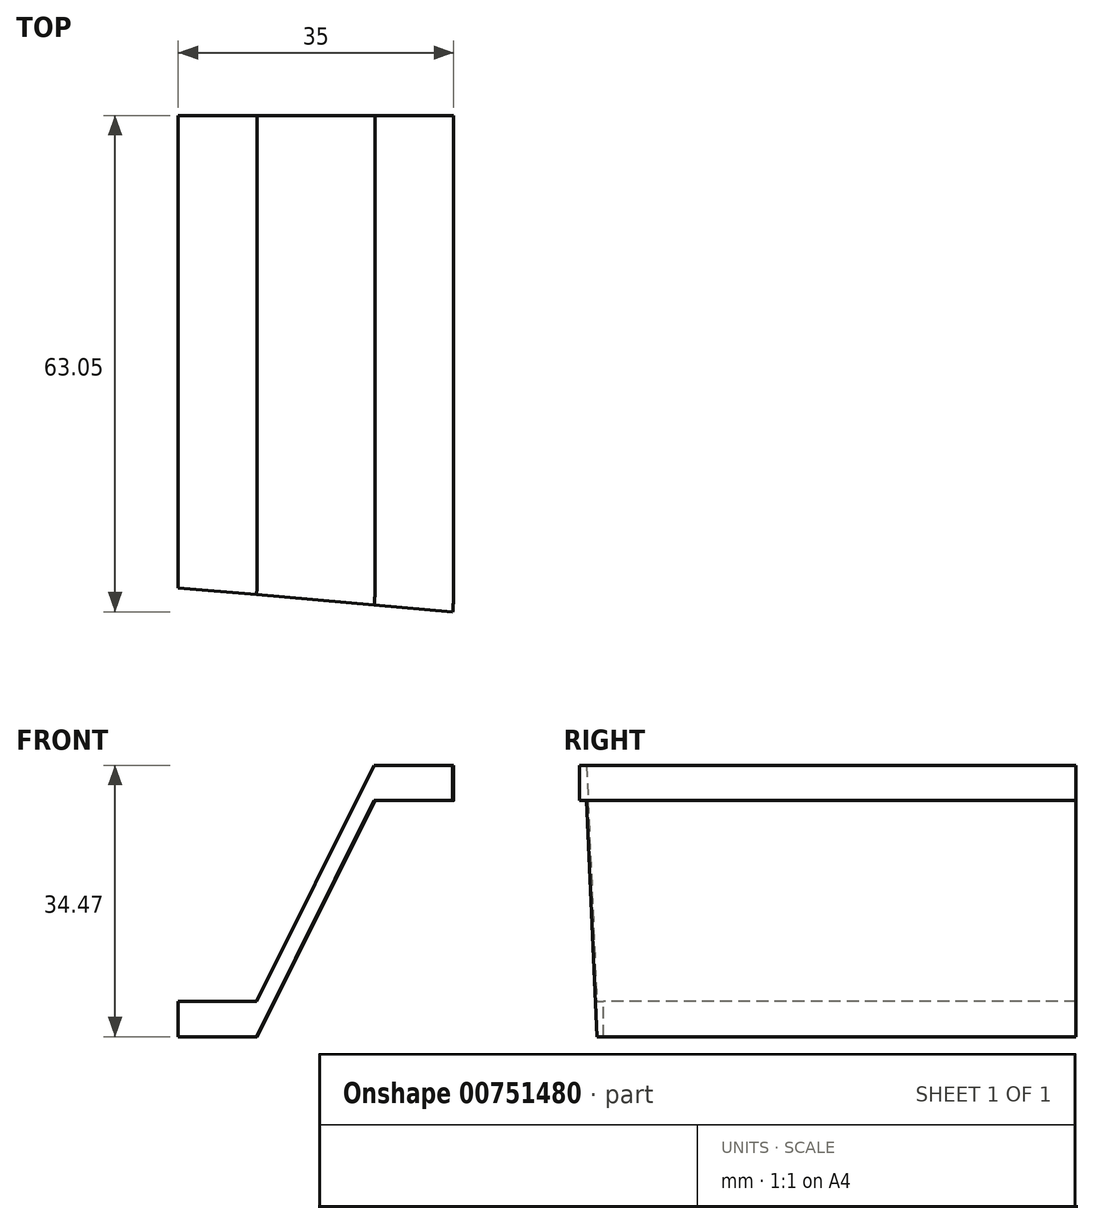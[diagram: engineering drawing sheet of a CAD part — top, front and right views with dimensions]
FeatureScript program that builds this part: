
annotation { "Feature Type Name" : "Feature", "Feature Type Description" : "" }
export const myFeature = defineFeature(function(context is Context, id is Id, definition is map)
    precondition{}
    {
        {
            var Q0;
            Q0=qCreatedBy(makeId("Front.planeOp"),FACE);
            cPlane(context, id + "F0", {"entities" : qUnion([Q0]), "cplaneType" : CPlaneType.OFFSET, "offset" : 30 * mm, "oppositeDirection" : true, "width" : 150 * mm, "height" : 150 * mm});
        }
        {
            var Q0;
            Q0=qCreatedBy(makeId("Front.planeOp"),FACE);
            cPlane(context, id + "F1", {"entities" : qUnion([Q0]), "cplaneType" : CPlaneType.OFFSET, "offset" : 30 * mm, "width" : 150 * mm, "height" : 150 * mm});
        }
        {
            var Q0;
            Q0=qCreatedBy(id+"F1.planeOp",FACE);
            var sketch = newSketch(context, id + "F2", { "sketchPlane" : qUnion([Q0])});
            skLineSegment(sketch, "E0.bottom", {"start": v(0, 34.47) * mm, "end": v(-10, 34.47) * mm});
            skLineSegment(sketch, "E0.top", {"start": v(0, 30) * mm, "end": v(-10, 30) * mm});
            skLineSegment(sketch, "E0.left", {"start": v(0, 34.47) * mm, "end": v(0, 30) * mm});
            skLineSegment(sketch, "E0.right", {"start": v(-10, 34.47) * mm, "end": v(-10, 30) * mm});
            skLineSegment(sketch, "E1.bottom", {"start": v(-25, 0) * mm, "end": v(-35, 0) * mm});
            skLineSegment(sketch, "E1.top", {"start": v(-25, 4.47) * mm, "end": v(-35, 4.47) * mm});
            skLineSegment(sketch, "E1.left", {"start": v(-25, 0) * mm, "end": v(-25, 4.47) * mm});
            skLineSegment(sketch, "E1.right", {"start": v(-35, 0) * mm, "end": v(-35, 4.47) * mm});
            skLineSegment(sketch, "E2", {"start": v(-25, 0) * mm, "end": v(-10, 30) * mm});
            skLineSegment(sketch, "E3", {"start": v(-10, 34.47) * mm, "end": v(-25, 4.47) * mm});
            skArc(sketch, "E4", {"start": v(-12.24, 30) * mm, "mid": v(-24.66, 23.05) * mm, "end": v(-22.76, 8.94) * mm});
            skArc(sketch, "E5.0", {"start": v(-11.28, 31.9) * mm, "mid": v(-26.44, 23.94) * mm, "end": v(-23.72, 7.04) * mm});
            skSolve(sketch);
        }
        {
            var Q0;
            Q0=qCreatedBy(makeId("Front.planeOp"),FACE);
            var sketch = newSketch(context, id + "F3", { "sketchPlane" : qUnion([Q0])});
            skLineSegment(sketch, "E6.bottom", {"start": v(0, 34.47) * mm, "end": v(-10, 34.47) * mm});
            skLineSegment(sketch, "E6.top", {"start": v(0, 30) * mm, "end": v(-10, 30) * mm});
            skLineSegment(sketch, "E6.left", {"start": v(0, 34.47) * mm, "end": v(0, 30) * mm});
            skLineSegment(sketch, "E6.right", {"start": v(-10, 34.47) * mm, "end": v(-10, 30) * mm});
            skLineSegment(sketch, "E7.bottom", {"start": v(-25, 0) * mm, "end": v(-35, 0) * mm});
            skLineSegment(sketch, "E7.top", {"start": v(-25, 4.47) * mm, "end": v(-35, 4.47) * mm});
            skLineSegment(sketch, "E7.left", {"start": v(-25, 0) * mm, "end": v(-25, 4.47) * mm});
            skLineSegment(sketch, "E7.right", {"start": v(-35, 0) * mm, "end": v(-35, 4.47) * mm});
            skLineSegment(sketch, "E8", {"start": v(-25, 0) * mm, "end": v(-10, 30) * mm});
            skLineSegment(sketch, "E9", {"start": v(-10, 34.47) * mm, "end": v(-25, 4.47) * mm});
            skArc(sketch, "E10", {"start": v(-13.58, 27.32) * mm, "mid": v(-20.18, 20.81) * mm, "end": v(-21.42, 11.63) * mm});
            skArc(sketch, "E11.0", {"start": v(-12.4, 29.67) * mm, "mid": v(-21.75, 21.6) * mm, "end": v(-22.6, 9.27) * mm});
            skSolve(sketch);
        }
        {
            var Q0;
            Q0=qCreatedBy(id+"F0.planeOp",FACE);
            var sketch = newSketch(context, id + "F4", { "sketchPlane" : qUnion([Q0])});
            skLineSegment(sketch, "E12.bottom", {"start": v(0, 34.47) * mm, "end": v(-10, 34.47) * mm});
            skLineSegment(sketch, "E12.top", {"start": v(0, 30) * mm, "end": v(-10, 30) * mm});
            skLineSegment(sketch, "E12.left", {"start": v(0, 34.47) * mm, "end": v(0, 30) * mm});
            skLineSegment(sketch, "E12.right", {"start": v(-10, 34.47) * mm, "end": v(-10, 30) * mm});
            skLineSegment(sketch, "E13.bottom", {"start": v(-25, 0) * mm, "end": v(-35, 0) * mm});
            skLineSegment(sketch, "E13.top", {"start": v(-25, 4.47) * mm, "end": v(-35, 4.47) * mm});
            skLineSegment(sketch, "E13.left", {"start": v(-25, 0) * mm, "end": v(-25, 4.47) * mm});
            skLineSegment(sketch, "E13.right", {"start": v(-35, 0) * mm, "end": v(-35, 4.47) * mm});
            skLineSegment(sketch, "E14", {"start": v(-25, 0) * mm, "end": v(-10, 30) * mm});
            skLineSegment(sketch, "E15", {"start": v(-10, 34.47) * mm, "end": v(-25, 4.47) * mm});
            skArc(sketch, "E16.0", {"start": v(-13.58, 27.32) * mm, "mid": v(-18.4, 19.92) * mm, "end": v(-21.42, 11.63) * mm});
            skSolve(sketch);
        }
        {
            var Q0;
            {var subQ1=sQuery(id+"F4.wireOp",EDGE,"E12.right");Q0=makeQuery(id+"F4.imprint","IMPRINT",FACE,{"disambiguationData":[TD([[makeQuery(id+"F4.imprint","IMPRINT",EDGE,{"derivedFrom":subQ1}),-1.0]])]});}
            var Q1;
            {var subQ1=sQuery(id+"F3.wireOp",EDGE,"E6.right");Q1=makeQuery(id+"F3.imprint","IMPRINT",FACE,{"disambiguationData":[TD([[makeQuery(id+"F3.imprint","IMPRINT",EDGE,{"derivedFrom":subQ1}),-1.0]])]});}
            var Q2;
            {var subQ1=sQuery(id+"F2.wireOp",EDGE,"E0.right");Q2=makeQuery(id+"F2.imprint","IMPRINT",FACE,{"disambiguationData":[TD([[makeQuery(id+"F2.imprint","IMPRINT",EDGE,{"derivedFrom":subQ1}),-1.0]])]});}
            loft(context, id + "F5", {"sheetProfilesArray" : [{ "sheetProfileEntities" : qUnion([Q0]) }, { "sheetProfileEntities" : qUnion([Q1]) }, { "sheetProfileEntities" : qUnion([Q2]) }]});
        }
        {
            var Q1;
            Q1=makeQuery(id+"F2.imprint","IMPRINT",FACE,{"disambiguationData":[TD([[makeQuery(id+"F2.imprint","IMPRINT",EDGE,{"derivedFrom":sQuery(id+"F2.wireOp",EDGE,"E0.bottom")}),1.0]])]});
            var Q2;
            Q2=makeQuery(id+"F3.imprint","IMPRINT",FACE,{"disambiguationData":[TD([[makeQuery(id+"F3.imprint","IMPRINT",EDGE,{"derivedFrom":sQuery(id+"F3.wireOp",EDGE,"E6.bottom")}),1.0]])]});
            var Q3;
            Q3=makeQuery(id+"F4.imprint","IMPRINT",FACE,{"disambiguationData":[TD([[makeQuery(id+"F4.imprint","IMPRINT",EDGE,{"derivedFrom":sQuery(id+"F4.wireOp",EDGE,"E12.bottom")}),1.0]])]});
            loft(context, id + "F6", {"operationType" : NewBodyOperationType.ADD, "sheetProfilesArray" : [{ "sheetProfileEntities" : qUnion([Q1]) }, { "sheetProfileEntities" : qUnion([Q2]) }, { "sheetProfileEntities" : qUnion([Q3]) }]});
        }
        {
            var Q1;
            Q1=makeQuery(id+"F2.imprint","IMPRINT",FACE,{"disambiguationData":[TD([[makeQuery(id+"F2.imprint","IMPRINT",EDGE,{"derivedFrom":sQuery(id+"F2.wireOp",EDGE,"E1.bottom")}),-1.0]])]});
            var Q2;
            Q2=makeQuery(id+"F3.imprint","IMPRINT",FACE,{"disambiguationData":[TD([[makeQuery(id+"F3.imprint","IMPRINT",EDGE,{"derivedFrom":sQuery(id+"F3.wireOp",EDGE,"E7.bottom")}),-1.0]])]});
            var Q3;
            Q3=makeQuery(id+"F4.imprint","IMPRINT",FACE,{"disambiguationData":[TD([[makeQuery(id+"F4.imprint","IMPRINT",EDGE,{"derivedFrom":sQuery(id+"F4.wireOp",EDGE,"E13.bottom")}),-1.0]])]});
            loft(context, id + "F7", {"operationType" : NewBodyOperationType.ADD, "sheetProfilesArray" : [{ "sheetProfileEntities" : qUnion([Q1]) }, { "sheetProfileEntities" : qUnion([Q2]) }, { "sheetProfileEntities" : qUnion([Q3]) }]});
        }
        {
            var Q0;
            {var subQ1=sQuery(id+"F2.wireOp",EDGE,"E0.right");Q0=makeQuery(id+"F2.imprint","IMPRINT",FACE,{"disambiguationData":[TD([[makeQuery(id+"F2.imprint","IMPRINT",EDGE,{"derivedFrom":subQ1}),-1.0]])]});}
            var Q1;
            Q1=makeQuery(id+"F2.imprint","IMPRINT",FACE,{"disambiguationData":[TD([[makeQuery(id+"F2.imprint","IMPRINT",EDGE,{"derivedFrom":sQuery(id+"F2.wireOp",EDGE,"E0.bottom")}),1.0]])]});
            var Q2;
            Q2=makeQuery(id+"F2.imprint","IMPRINT",FACE,{"disambiguationData":[TD([[makeQuery(id+"F2.imprint","IMPRINT",EDGE,{"derivedFrom":sQuery(id+"F2.wireOp",EDGE,"E1.bottom")}),-1.0]])]});
            var Q3;
            Q3=sQuery(id+"F2.wireOp",EDGE,"E1.right");
            revolve(context, id + "F8", {"operationType" : NewBodyOperationType.ADD, "surfaceOperationType" : NewSurfaceOperationType.NEW, "entities" : qUnion([Q0, Q1, Q2]), "axis" : qUnion([Q3]), "revolveType" : RevolveType.ONE_DIRECTION, "oppositeDirection" : true, "angle" : 5 * degree});
        }
    });
